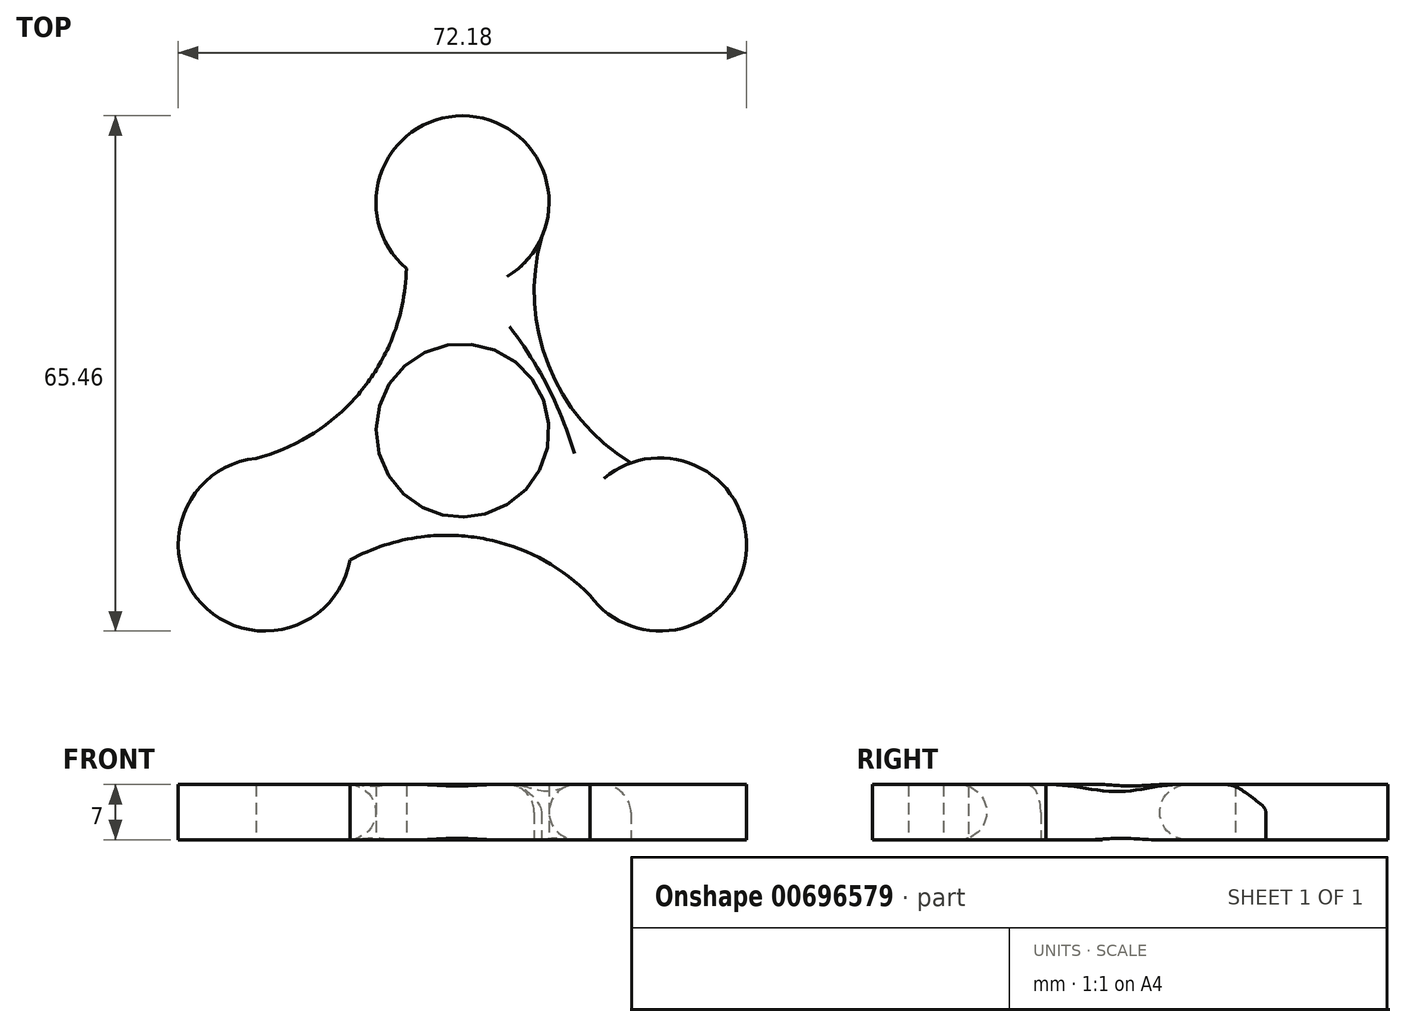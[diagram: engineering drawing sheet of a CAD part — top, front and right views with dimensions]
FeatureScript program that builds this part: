
annotation { "Feature Type Name" : "Feature", "Feature Type Description" : "" }
export const myFeature = defineFeature(function(context is Context, id is Id, definition is map)
    precondition{}
    {
        {
            var Q0;
            Q0=qCreatedBy(makeId("Top.planeOp"),FACE);
            var sketch = newSketch(context, id + "F0", { "sketchPlane" : qUnion([Q0])});
            skCircle(sketch, "E0", {"center": v(0, 0) * mm, "radius": 11 * mm});
            skCircle(sketch, "E1", {"center": v(0, 28.97) * mm, "radius": 11 * mm});
            skCircle(sketch, "E2.1.0", {"center": v(-25.1, -14.49) * mm, "radius": 11 * mm});
            skCircle(sketch, "E2.2.0", {"center": v(25.1, -14.49) * mm, "radius": 11 * mm});
            skArc(sketch, "E3", {"start": v(10.05, 24.5) * mm, "mid": v(10.91, 8.28) * mm, "end": v(21.4, -4.13) * mm});
            skArc(sketch, "E4.1.0", {"start": v(-26.24, -3.55) * mm, "mid": v(-12.63, 5.3) * mm, "end": v(-7.12, 20.6) * mm});
            skArc(sketch, "E4.2.0", {"start": v(16.2, -20.95) * mm, "mid": v(1.71, -13.59) * mm, "end": v(-14.27, -16.47) * mm});
            skSolve(sketch);
        }
        {
            var Q0;
            Q0=makeQuery(id+"F0.imprint","IMPRINT",FACE,{"disambiguationData":[TD([[makeQuery(id+"F0.imprint","IMPRINT",EDGE,{"derivedFrom":sQuery(id+"F0.wireOp",EDGE,"E0")}),-1.0]])]});
            var Q1;
            Q1 = qSketchRegion(id + "F0", true);
            extrude(context, id + "F1", {"entities" : qUnion([Q0, Q1]), "depth" : 7 * mm, "offsetDistance" : 25 * mm});
        }
        {
            var Q0;
            Q0=makeQuery(id+"F1.opExtrude","CAP_EDGE",EDGE,{"disambiguationData":[OSD([sQuery(id+"F0.wireOp",EDGE,"E3")])],"isStart":false});
            var Q1;
            Q1=makeQuery(id+"F1.opExtrude","SWEPT_FACE",FACE,{"disambiguationData":[OSD([sQuery(id+"F0.wireOp",EDGE,"E0")])]});
            fillet(context, id + "F2", {"entities" : qUnion([Q0, Q1]), "radius" : 3.5 * mm, "tangentPropagation" : true, "allowEdgeOverflow" : false});
        }
    });
